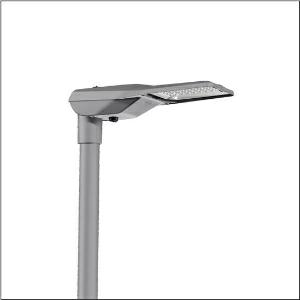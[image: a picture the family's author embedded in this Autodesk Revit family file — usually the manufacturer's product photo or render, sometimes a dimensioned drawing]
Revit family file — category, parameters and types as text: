
# Revit family: streetlight_sl_21_iq_mini___st1_0a_5xe2d21y08hb_5d36
name_source: partatom
category: Lighting Fixtures
units: mm (PartAtom-declared; Revit-internal decimal feet)

## family parameters
Cut with Voids When Loaded = No
Host = Face
Light Source = No
Part Type = Normal
Room Calculation Point = No
Round Connector Dimension = Use Diameter
Shared = No

## types (1)
- --- (1 x LED, 7820 lm, 71 W, 2200K)
    Apparent Load = 71 VA
    CIE Flux Codes = 37 72 97 100 100
    Color Rendering = 70
    Color Temperature = 2200K
    Default Elevation = 1800 mm
    Description = Streetlight SL 21 iQ mini, mast luminaire, primary light control with lens, of PMMA, primary optical cover: cover, of toughened safety glass, transparent, light distribution: ST1.0a, light emission: direct distribution, primary light characteristic: asymmetric, installation type: post-top, side-entry, LED, High Power LED, rated luminous flux: 7.820lm, luminous efficacy: 110lm/W, light colour: 722, colour temperature: 2200K, control: presetting dimming logarithmic, Street-Remote, Auto-Match, Temp-Guard, Lumen-Switch, Night-Set, Smart-Wire, Light-Fading, Desk-Remote (wireless, voltage-free reading and setting of iQ features in the workshop via application-optimized NFC function/RFID function), optimised constant luminous flux control (CLO 2.0), mains connection: 220..240V, AC, 50/60Hz, start of lifetime: 71W, end of service life: 75W, reduction: 30W, luminaire housing, of diecast aluminium, powder-coated, Siteco® metallic grey (DB 702S), corrosivity category C5 mid according to DIN EN ISO 12944, please order mast flange separately, inclination adjustable: 0°, 5°, 10°, 15°, sealing non-destructively replaceable, multi-level sealing system, length: 628mm, width: 235mm, height: 110mm, mast flange for spigot size: 42mm (side-entry): 5XC10008XM4, 60/48mm (side-entry/post-top): 5XC10108XM2, 76/60mm (side-entry/post-top): 5XC10108XM1, Smart Interface below and above, protection rating (complete): IP66, insulation class (complete): insulation class II (safety insulation), certification: CE, ENEC, ENEC+, VDE, impact resistance: IK09, permissible operating ambient temperature for outdoor applications: -40..+50°C, standard-compliant lighting for roads and squares, packaging unit: 1 piece

Light Distribution: ST1.0a
    Height = 110 mm
    Lamp = 1 x LED
    Lamp Light Flux = 7820 lm
    Lamp Power = 71 W
    Lamp count = 1
    Length = 625 mm
    Luminous efficacy = 110 lm/W
    Manufacturer = Siteco
    ModVariant = No
    Model = 5XE2D21Y08HB
    Number of Poles = 1
    OnlyDefault = Yes
    Power Factor = 1
    Product Name = Streetlight SL 21 iQ mini | ST1.0a
    Product group = mast luminaire | pylon top
    ProductGroupID = 6100
    Protection Class = Protection class II
    Protection Degree = IP 66
    RLX_Detail_Level = 1
    RLX_Emergency_Light_Flux = 0 lm
    RLX_Emergency_Type = 0
    RLX_Emergency_Type_DB = No
    RlxData = <blob elided: 92353 chars, md5=41624001>
    Socket = socket
    Standby Power = 0 W
    System Light Flux = 7820 lm
    System Power = 71 W
    Type Comments = factory setting: luminous flux: 100 % | dim-lin: 254 | 716 mA
    Type Image = l_1003514.jpg
    URL = http://relux.com
    VarID = @adj_045071
    Voltage = 0 V
    Weight = 0.00 kg
    Width = 234 mm

## geometry (parser evidence)
native form markers: Blend x4, Sweep x12
no freeform markers — native parametric forms only
